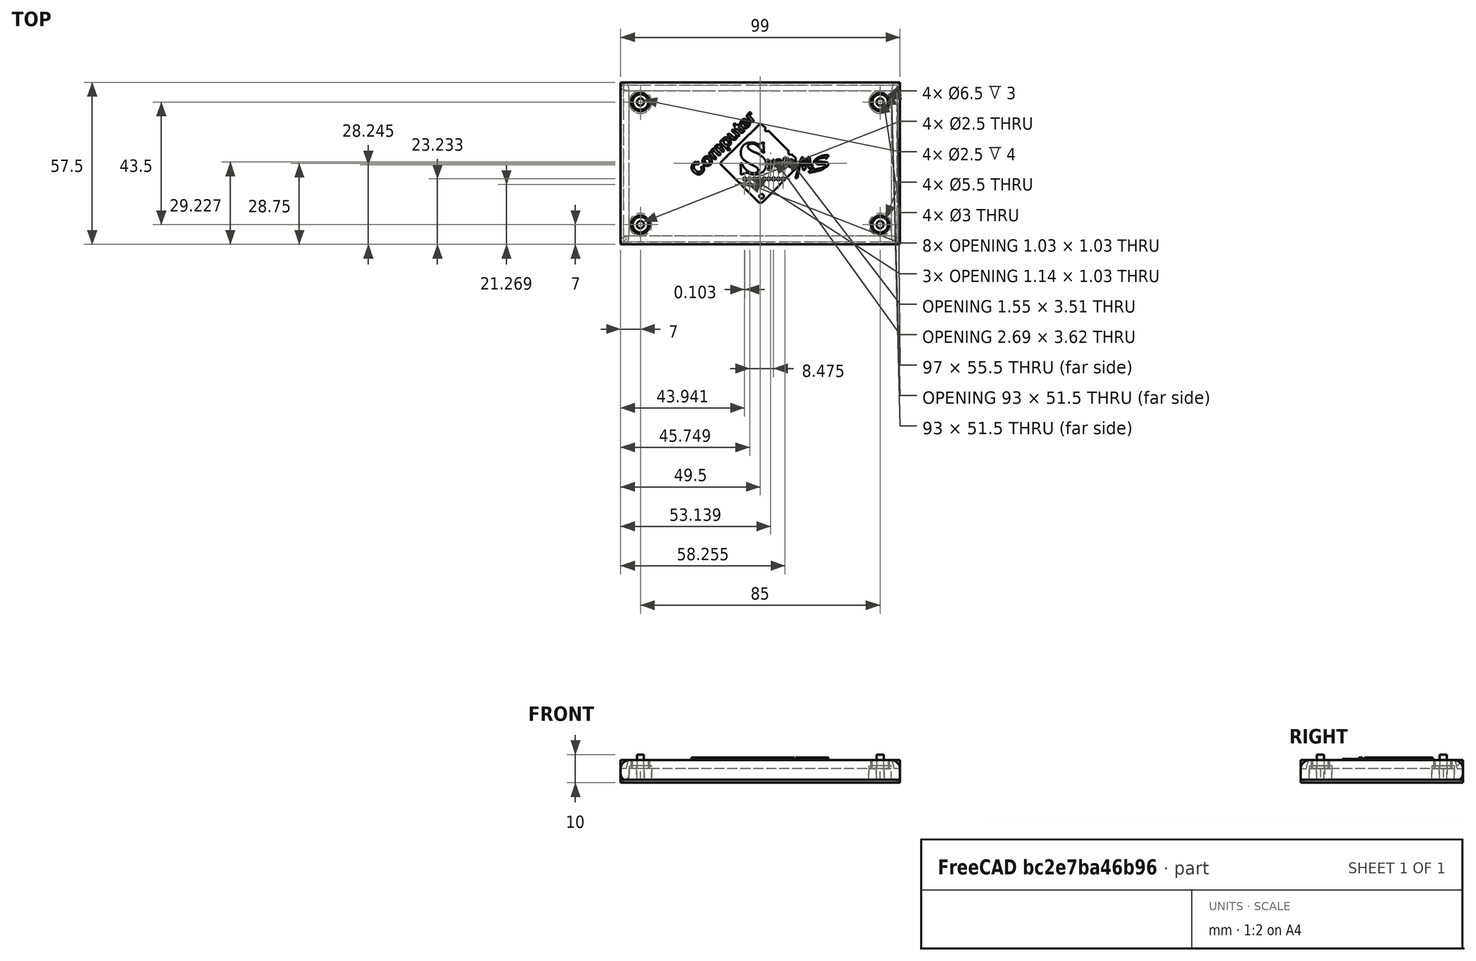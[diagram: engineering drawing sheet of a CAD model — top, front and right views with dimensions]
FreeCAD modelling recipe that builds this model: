
FCSTD DOCUMENT  (FreeCAD 0.15R4572 (Git))
Label: top2
License: All rights reserved
LicenseURL: http://en.wikipedia.org/wiki/All_rights_reserved
objects: Part::Feature×32, Part::Extrusion×32, Sketcher::SketchObject×10, Part::Cut×5, PartDesign::Pad×4, PartDesign::Fillet×4, PartDesign::Pocket×3, Part::Thickness×1, Part::MultiFuse×1
note: 99 computed .brp shape members not serialized (recipe doc carries the construction recipe); baked Part::Feature solids carry a one-line shape summary decoded from their .brp

FEATURE [Sketcher::SketchObject] Sketch  label="Отверстия под части корпуса"
  sketch-geometry (12):
    g0: LineSegment [constr] StartX=-42.5 StartY=21.75 StartZ=0 EndX=42.5 EndY=21.75 EndZ=0
    g1: LineSegment [constr] StartX=42.5 StartY=21.75 StartZ=0 EndX=42.5 EndY=-21.75 EndZ=0
    g2: LineSegment [constr] StartX=42.5 StartY=-21.75 StartZ=0 EndX=-42.5 EndY=-21.75 EndZ=0
    g3: LineSegment [constr] StartX=-42.5 StartY=-21.75 StartZ=0 EndX=-42.5 EndY=21.75 EndZ=0
    g4: Circle CenterX=-42.5 CenterY=21.75 CenterZ=0 NormalX=0 NormalY=0 NormalZ=1 Radius=1.5
    g5: Circle CenterX=-42.5 CenterY=21.75 CenterZ=0 NormalX=0 NormalY=0 NormalZ=1 Radius=4
    g6: Circle CenterX=-42.5 CenterY=-21.75 CenterZ=0 NormalX=0 NormalY=0 NormalZ=1 Radius=1.5
    g7: Circle CenterX=42.5 CenterY=-21.75 CenterZ=0 NormalX=0 NormalY=0 NormalZ=1 Radius=1.5
    g8: Circle CenterX=42.5 CenterY=21.75 CenterZ=0 NormalX=0 NormalY=0 NormalZ=1 Radius=1.5
    g9: Circle CenterX=-42.5 CenterY=-21.75 CenterZ=0 NormalX=0 NormalY=0 NormalZ=1 Radius=4
    g10: Circle CenterX=42.5 CenterY=-21.75 CenterZ=0 NormalX=0 NormalY=0 NormalZ=1 Radius=4
    g11: Circle CenterX=42.5 CenterY=21.75 CenterZ=0 NormalX=0 NormalY=0 NormalZ=1 Radius=4
  constraints (28):
    c: Coincident(g0,g1)
    c: Coincident(g1,g2)
    c: Coincident(g2,g3)
    c: Coincident(g3,g0)
    c: Horizontal(g0)
    c: Horizontal(g2)
    c: Vertical(g1)
    c: Vertical(g3)
    c: Symmetric(g1,g0,g-1)
    c: Symmetric(g0,g0,g-2)
    c: DistanceY(g1) = -43.5
    c: DistanceX(g0) = 85
    c: Coincident(g4,g0)
    c: Coincident(g5,g0)
    c: Coincident(g6,g2)
    c: Coincident(g7,g1)
    c: Coincident(g8,g0)
    c: Equal(g8,g7)
    c: Equal(g7,g6)
    c: Equal(g6,g4)
    c: Radius(g7) = 1.5
    c: Coincident(g9,g2)
    c: Coincident(g10,g1)
    c: Coincident(g11,g0)
    c: Equal(g11,g10)
    c: Equal(g10,g9)
    c: Equal(g9,g5)
    c: Radius(g9) = 4
FEATURE [Sketcher::SketchObject] Sketch001  label="Маска нижней части"
  sketch-geometry (8):
    g0: LineSegment [constr] StartX=-45 StartY=25 StartZ=0 EndX=45 EndY=25 EndZ=0
    g1: LineSegment [constr] StartX=45 StartY=25 StartZ=0 EndX=45 EndY=-25 EndZ=0
    g2: LineSegment [constr] StartX=45 StartY=-25 StartZ=0 EndX=-45 EndY=-25 EndZ=0
    g3: LineSegment [constr] StartX=-45 StartY=-25 StartZ=0 EndX=-45 EndY=25 EndZ=0
    g4: LineSegment StartX=-46.5 StartY=25.75 StartZ=0 EndX=46.5 EndY=25.75 EndZ=0
    g5: LineSegment StartX=46.5 StartY=25.75 StartZ=0 EndX=46.5 EndY=-25.75 EndZ=0
    g6: LineSegment StartX=46.5 StartY=-25.75 StartZ=0 EndX=-46.5 EndY=-25.75 EndZ=0
    g7: LineSegment StartX=-46.5 StartY=-25.75 StartZ=0 EndX=-46.5 EndY=25.75 EndZ=0
  constraints (24):
    c: Coincident(g0,g1)
    c: Coincident(g1,g2)
    c: Coincident(g2,g3)
    c: Coincident(g3,g0)
    c: Horizontal(g0)
    c: Horizontal(g2)
    c: Vertical(g1)
    c: Vertical(g3)
    c: Symmetric(g0,g0,g-2)
    c: Symmetric(g0,g1,g-1)
    c: DistanceX(g0) = 90
    c: DistanceY(g1) = -50
    c: Coincident(g4,g5)
    c: Coincident(g5,g6)
    c: Coincident(g6,g7)
    c: Coincident(g7,g4)
    c: Horizontal(g4)
    c: Horizontal(g6)
    c: Vertical(g5)
    c: Vertical(g7)
    c: Symmetric(g4,g5,g-1)
    c: Symmetric(g4,g4,g-2)
    c: DistanceY(g7) = 51.5
    c: DistanceX(g6) = -93
FEATURE [PartDesign::Pad] Pad
  Length = 4
  Length2 = 100
  Sketch = -> Sketch001
  Type = 0
FEATURE [Part::Thickness] Thickness
  Faces = -> Pad [Face5]
  Intersection = false
  Join = 2
  Mode = 0
  SelfIntersection = false
  Value = 3
FEATURE [PartDesign::Pad] Pad001
  Length = 5
  Length2 = 100
  Sketch = -> Sketch
  Type = 0
FEATURE [Sketcher::SketchObject] Sketch002  label="Отверстия под части корпуса001"
  Placement = pos=(0,0,7) rot=(0,0,1;0rad)
  Support = -> Thickness [Face11]
  sketch-geometry (8):
    g0: LineSegment [constr] StartX=-42.5 StartY=21.75 StartZ=0 EndX=42.5 EndY=21.75 EndZ=0
    g1: LineSegment [constr] StartX=42.5 StartY=21.75 StartZ=0 EndX=42.5 EndY=-21.75 EndZ=0
    g2: LineSegment [constr] StartX=42.5 StartY=-21.75 StartZ=0 EndX=-42.5 EndY=-21.75 EndZ=0
    g3: LineSegment [constr] StartX=-42.5 StartY=-21.75 StartZ=0 EndX=-42.5 EndY=21.75 EndZ=0
    g4: Circle CenterX=-42.5 CenterY=21.75 CenterZ=0 NormalX=0 NormalY=0 NormalZ=1 Radius=2.75
    g5: Circle CenterX=-42.5 CenterY=-21.75 CenterZ=0 NormalX=0 NormalY=0 NormalZ=1 Radius=2.75
    g6: Circle CenterX=42.5 CenterY=-21.75 CenterZ=0 NormalX=0 NormalY=0 NormalZ=1 Radius=2.75
    g7: Circle CenterX=42.5 CenterY=21.75 CenterZ=0 NormalX=0 NormalY=0 NormalZ=1 Radius=2.75
  constraints (20):
    c: Coincident(g0,g1)
    c: Coincident(g1,g2)
    c: Coincident(g2,g3)
    c: Coincident(g3,g0)
    c: Horizontal(g0)
    c: Horizontal(g2)
    c: Vertical(g1)
    c: Vertical(g3)
    c: Symmetric(g1,g0,g-1)
    c: Symmetric(g0,g0,g-2)
    c: DistanceY(g1) = -43.5
    c: DistanceX(g0) = 85
    c: Coincident(g4,g0)
    c: Coincident(g5,g2)
    c: Coincident(g6,g1)
    c: Coincident(g7,g0)
    c: Equal(g7,g6)
    c: Equal(g6,g5)
    c: Equal(g5,g4)
    c: Radius(g6) = 2.75
FEATURE [PartDesign::Pocket] Pocket
  Length = 3.5
  Sketch = -> Sketch002
  Type = 0
FEATURE [Part::Feature] Face
  shape: bbox 1.861 x 1.858 x 2e-07 mm, 1 faces, 0 solids (baked)
FEATURE [Part::Feature] Face001
  shape: bbox 9.096 x 11.37 x 2e-07 mm, 1 faces, 0 solids (baked)
FEATURE [Part::Feature] Face002
  shape: bbox 1.758 x 1.861 x 2e-07 mm, 1 faces, 0 solids (baked)
FEATURE [Part::Feature] Face003
  shape: bbox 1.035 x 1.032 x 2e-07 mm, 1 faces, 0 solids (baked)
FEATURE [Part::Feature] Face004
  shape: bbox 1.035 x 1.032 x 2e-07 mm, 1 faces, 0 solids (baked)
FEATURE [Part::Feature] Face005
  shape: bbox 1.138 x 1.032 x 2e-07 mm, 1 faces, 0 solids (baked)
FEATURE [Part::Feature] Face006
  shape: bbox 1.032 x 1.032 x 2e-07 mm, 1 faces, 0 solids (baked)
FEATURE [Part::Feature] Face007
  shape: bbox 1.035 x 1.032 x 2e-07 mm, 1 faces, 0 solids (baked)
FEATURE [Part::Feature] Face008
  shape: bbox 4.445 x 4.548 x 2e-07 mm, 1 faces, 0 solids (baked)
FEATURE [Part::Extrusion] Extrude003
  Base = -> Face005
  Dir = (0,0,1)
  Solid = false
FEATURE [Part::Extrusion] Extrude004
  Base = -> Face004
  Dir = (0,0,1)
  Solid = false
FEATURE [Part::Extrusion] Extrude005
  Base = -> Face006
  Dir = (0,0,1)
  Solid = false
FEATURE [Part::Extrusion] Extrude010
  Base = -> Face007
  Dir = (0,0,1)
  Solid = false
FEATURE [Part::Extrusion] Extrude012
  Base = -> Face
  Dir = (0,0,1)
  Solid = false
FEATURE [Part::Extrusion] Extrude013  label="C"
  Base = -> Face008
  Dir = (0,0,1)
  Solid = true
FEATURE [Part::Feature] Face009
  shape: bbox 3.431 x 3.472 x 2e-07 mm, 1 faces, 0 solids (baked)
FEATURE [Part::Extrusion] Extrude
  Base = -> Face009
  Dir = (0,0,1)
  Solid = false
FEATURE [Part::Feature] Face010
  shape: bbox 5.686 x 5.271 x 2e-07 mm, 1 faces, 0 solids (baked)
FEATURE [Part::Extrusion] Extrude014  label="M"
  Base = -> Face010
  Dir = (0,0,1)
  Solid = false
FEATURE [Part::Cut] Cut  label="O"
  Base = -> Extrude
  Tool = -> Extrude012
FEATURE [Part::Feature] Face011
  shape: bbox 6.013 x 7.647 x 2e-07 mm, 1 faces, 0 solids (baked)
FEATURE [Part::Feature] Face012
  shape: bbox 6.923 x 6.2 x 2e-07 mm, 1 faces, 0 solids (baked)
FEATURE [Part::Feature] Face013
  shape: bbox 1.032 x 0.6202 x 2e-07 mm, 1 faces, 0 solids (baked)
FEATURE [Part::Feature] Face014
  shape: bbox 2.375 x 2.687 x 2e-07 mm, 1 faces, 0 solids (baked)
FEATURE [Part::Feature] Face015
  shape: bbox 1.549 x 3.513 x 2e-07 mm, 1 faces, 0 solids (baked)
FEATURE [Part::Feature] Face016
  shape: bbox 2.478 x 2.687 x 2e-07 mm, 1 faces, 0 solids (baked)
FEATURE [Part::Feature] Face017
  shape: bbox 2.687 x 3.619 x 2e-07 mm, 1 faces, 0 solids (baked)
FEATURE [Part::Extrusion] Extrude015  label="S"
  Base = -> Face001
  Dir = (0,0,1)
  Solid = false
FEATURE [Part::Extrusion] Extrude016  label="S002"
  Base = -> Face016
  Dir = (0,0,1)
  Solid = false
FEATURE [Part::Extrusion] Extrude017
  Base = -> Face014
  Dir = (0,0,1)
  Solid = false
FEATURE [Part::Extrusion] Extrude018
  Base = -> Face013
  Dir = (0,0,1)
  Solid = false
FEATURE [Part::Extrusion] Extrude019
  Base = -> Face002
  Dir = (0,0,1)
  Solid = false
FEATURE [Part::Extrusion] Extrude020  label="S001"
  Base = -> Face012
  Dir = (0,0,1)
  Solid = false
FEATURE [Part::Extrusion] Extrude022  label="T001"
  Base = -> Face015
  Dir = (0,0,1)
  Solid = false
FEATURE [Part::Extrusion] Extrude023  label="M001"
  Base = -> Face011
  Dir = (0,0,1)
  Solid = false
FEATURE [Part::Extrusion] Extrude024  label="Y"
  Base = -> Face017
  Dir = (0,0,1)
  Solid = false
FEATURE [Part::Feature] Face018
  shape: bbox 26.62 x 28.11 x 2e-07 mm, 1 faces, 0 solids (baked)
FEATURE [Part::Extrusion] Extrude001
  Base = -> Face018
  Dir = (0,0,0.5)
  Solid = false
FEATURE [Part::Feature] Face019
  shape: bbox 3.97 x 4.859 x 2e-07 mm, 1 faces, 0 solids (baked)
FEATURE [Part::Extrusion] Extrude021
  Base = -> Face019
  Dir = (0,0,1)
  Solid = false
FEATURE [Part::Feature] Face020
  shape: bbox 1.964 x 1.964 x 2e-07 mm, 1 faces, 0 solids (baked)
FEATURE [Part::Extrusion] Extrude007
  Base = -> Face020
  Dir = (0,0,1)
  Solid = false
FEATURE [Part::Cut] Cut001  label="P"
  Base = -> Extrude021
  Tool = -> Extrude019
FEATURE [Part::Cut] Cut002
  Base = -> Extrude001
  Tool = -> Extrude007
FEATURE [Part::Cut] Cut004  label="E001"
  Base = -> Extrude017
  Tool = -> Extrude018
FEATURE [Part::Feature] Face021
  shape: bbox 4.342 x 3.928 x 2e-07 mm, 1 faces, 0 solids (baked)
FEATURE [Part::Extrusion] Extrude011  label="U"
  Base = -> Face021
  Dir = (0,0,1)
  Solid = false
FEATURE [Part::Feature] Face022
  shape: bbox 3.822 x 3.513 x 2e-07 mm, 1 faces, 0 solids (baked)
FEATURE [Part::Extrusion] Extrude006  label="T"
  Base = -> Face022
  Dir = (0,0,1)
  Solid = false
FEATURE [Part::Feature] Face023
  shape: bbox 3.41 x 3.39 x 2e-07 mm, 1 faces, 0 solids (baked)
FEATURE [Part::Extrusion] Extrude008
  Base = -> Face023
  Dir = (0,0,1)
  Solid = false
FEATURE [Part::Feature] Face024
  shape: bbox 1.138 x 1.241 x 2e-07 mm, 1 faces, 0 solids (baked)
FEATURE [Part::Extrusion] Extrude009
  Base = -> Face024
  Dir = (0,0,1)
  Solid = false
FEATURE [Part::Cut] Cut003  label="E"
  Base = -> Extrude008
  Tool = -> Extrude009
FEATURE [Part::Feature] Face025
  shape: bbox 2.896 x 3.719 x 2e-07 mm, 1 faces, 0 solids (baked)
FEATURE [Part::Extrusion] Extrude002  label="R"
  Base = -> Face025
  Dir = (0,0,1)
  Solid = false
FEATURE [Part::Feature] Face026
  shape: bbox 1.035 x 1.032 x 2e-07 mm, 1 faces, 0 solids (baked)
FEATURE [Part::Feature] Face027
  shape: bbox 1.032 x 1.032 x 2e-07 mm, 1 faces, 0 solids (baked)
FEATURE [Part::Feature] Face028
  shape: bbox 1.138 x 1.032 x 2e-07 mm, 1 faces, 0 solids (baked)
FEATURE [Part::Feature] Face029
  shape: bbox 1.032 x 1.032 x 2e-07 mm, 1 faces, 0 solids (baked)
FEATURE [Part::Feature] Face030
  shape: bbox 1.138 x 1.032 x 2e-07 mm, 1 faces, 0 solids (baked)
FEATURE [Part::Feature] Face031
  shape: bbox 1.032 x 1.032 x 2e-07 mm, 1 faces, 0 solids (baked)
FEATURE [Part::Extrusion] Extrude025
  Base = -> Face031
  Dir = (0,0,1)
  Solid = false
FEATURE [Part::Extrusion] Extrude026
  Base = -> Face030
  Dir = (0,0,1)
  Solid = false
FEATURE [Part::Extrusion] Extrude027
  Base = -> Face029
  Dir = (0,0,1)
  Solid = false
FEATURE [Part::Extrusion] Extrude028
  Base = -> Face028
  Dir = (0,0,1)
  Solid = false
FEATURE [Part::Extrusion] Extrude029
  Base = -> Face027
  Dir = (0,0,1)
  Solid = false
FEATURE [Part::Extrusion] Extrude030
  Base = -> Face026
  Dir = (0,0,1)
  Solid = false
FEATURE [Part::Extrusion] Extrude031
  Base = -> Face003
  Dir = (0,0,1)
  Solid = false
FEATURE [Part::MultiFuse] Fusion
  Placement = pos=(-94,191,6.9) rot=(0,0,1;0rad)
  Shapes = -> [Extrude002,Extrude024,Extrude029,Extrude023,Extrude025,Extrude027,Extrude026,Extrude030,Extrude028,Extrude031,Cut002,Cut003,Cut004,Cut,Cut001,Extrude013,Extrude016,Extrude022,Extrude005,Extrude020,Extrude004,Extrude003,Extrude014,Extrude010,Extrude006,Extrude015,Extrude011]
FEATURE [Sketcher::SketchObject] Sketch003
  Placement = pos=(0,0,7) rot=(0,0,1;0rad)
  Support = -> Pocket [Face15]
  sketch-geometry (6):
    g0: LineSegment StartX=-48.8866 StartY=28.9301 StartZ=0 EndX=46.8488 EndY=28.9301 EndZ=0
    g1: LineSegment StartX=46.8488 StartY=28.9301 StartZ=0 EndX=46.8488 EndY=-28.4828 EndZ=0
    g2: LineSegment StartX=46.8488 StartY=-28.4828 StartZ=0 EndX=-48.8866 EndY=-28.4828 EndZ=0
    g3: LineSegment StartX=-48.8866 StartY=-28.4828 StartZ=0 EndX=-48.8866 EndY=28.9301 EndZ=0
    g4: LineSegment StartX=-48.8866 StartY=0 StartZ=0 EndX=46.8488 EndY=0 EndZ=0
    g5: LineSegment StartX=0 StartY=28.9301 StartZ=0 EndX=0 EndY=-28.4828 EndZ=0
  constraints (14):
    c: Coincident(g0,g1)
    c: Coincident(g1,g2)
    c: Coincident(g2,g3)
    c: Coincident(g3,g0)
    c: Horizontal(g0)
    c: Horizontal(g2)
    c: Vertical(g1)
    c: Vertical(g3)
    c: PointOnObject(g4,g3)
    c: PointOnObject(g4,g1)
    c: Horizontal(g4)
    c: PointOnObject(g5,g0)
    c: PointOnObject(g5,g2)
    c: Vertical(g5)
FEATURE [Sketcher::SketchObject] Sketch004
  Placement = pos=(-94,191,7.4) rot=(0,0,1;0rad)
  Support = -> Fusion [Face70]
FEATURE [Sketcher::SketchObject] Sketch005
  Placement = pos=(-94,191,7.4) rot=(0,0,1;0rad)
  Support = -> Fusion [Face70]
  sketch-geometry (4):
    g0: LineSegment StartX=69.5836 StartY=-172.746 StartZ=0 EndX=118.185 EndY=-172.746 EndZ=0
    g1: LineSegment StartX=118.185 StartY=-172.746 StartZ=0 EndX=118.185 EndY=-205.174 EndZ=0
    g2: LineSegment StartX=118.185 StartY=-205.174 StartZ=0 EndX=69.5836 EndY=-205.174 EndZ=0
    g3: LineSegment StartX=69.5836 StartY=-205.174 StartZ=0 EndX=69.5836 EndY=-172.746 EndZ=0
  constraints (8):
    c: Coincident(g0,g1)
    c: Coincident(g1,g2)
    c: Coincident(g2,g3)
    c: Coincident(g3,g0)
    c: Horizontal(g0)
    c: Horizontal(g2)
    c: Vertical(g1)
    c: Vertical(g3)
FEATURE [PartDesign::Fillet] Fillet
  Base = -> Pocket [Edge23,Edge25,Edge28,Edge26]
  Radius = 3
FEATURE [PartDesign::Fillet] Fillet001
  Base = -> Fillet [Edge1,Edge7,Edge17,Edge4]
  Radius = 2
FEATURE [Sketcher::SketchObject] Sketch006  label="Маска нижней части001"
  Placement = pos=(0,0,0) rot=(1,0,0;3.14159rad)
  Support = -> Thickness [Face6]
  sketch-geometry (8):
    g0: LineSegment StartX=-48.5 StartY=27.75 StartZ=0 EndX=48.5 EndY=27.75 EndZ=0
    g1: LineSegment StartX=48.5 StartY=27.75 StartZ=0 EndX=48.5 EndY=-27.75 EndZ=0
    g2: LineSegment StartX=48.5 StartY=-27.75 StartZ=0 EndX=-48.5 EndY=-27.75 EndZ=0
    g3: LineSegment StartX=-48.5 StartY=-27.75 StartZ=0 EndX=-48.5 EndY=27.75 EndZ=0
    g4: LineSegment StartX=-49.5 StartY=28.75 StartZ=0 EndX=49.5 EndY=28.75 EndZ=0
    g5: LineSegment StartX=49.5 StartY=28.75 StartZ=0 EndX=49.5 EndY=-28.75 EndZ=0
    g6: LineSegment StartX=49.5 StartY=-28.75 StartZ=0 EndX=-49.5 EndY=-28.75 EndZ=0
    g7: LineSegment StartX=-49.5 StartY=-28.75 StartZ=0 EndX=-49.5 EndY=28.75 EndZ=0
  constraints (24):
    c: Coincident(g0,g1)
    c: Coincident(g1,g2)
    c: Coincident(g2,g3)
    c: Coincident(g3,g0)
    c: Horizontal(g0)
    c: Horizontal(g2)
    c: Vertical(g1)
    c: Vertical(g3)
    c: Symmetric(g0,g0,g-2)
    c: Symmetric(g0,g1,g-1)
    c: DistanceX(g0) = 97
    c: DistanceY(g1) = -55.5
    c: Coincident(g4,g5)
    c: Coincident(g5,g6)
    c: Coincident(g6,g7)
    c: Coincident(g7,g4)
    c: Horizontal(g4)
    c: Horizontal(g6)
    c: Vertical(g5)
    c: Vertical(g7)
    c: Symmetric(g4,g5,g-1)
    c: Symmetric(g4,g4,g-2)
    c: DistanceY(g7) = 57.5
    c: DistanceX(g6) = -99
FEATURE [PartDesign::Pad] Pad002
  Length = 1
  Length2 = 100
  Sketch = -> Sketch006
  Type = 0
FEATURE [Sketcher::SketchObject] Sketch007  label="Отверстия под части корпуса002"
  Placement = pos=(0,0,4) rot=(1,0,0;3.14159rad)
  Support = -> Pad002 [Face5]
  sketch-geometry (12):
    g0: LineSegment [constr] StartX=-42.5 StartY=21.75 StartZ=0 EndX=42.5 EndY=21.75 EndZ=0
    g1: LineSegment [constr] StartX=42.5 StartY=21.75 StartZ=0 EndX=42.5 EndY=-21.75 EndZ=0
    g2: LineSegment [constr] StartX=42.5 StartY=-21.75 StartZ=0 EndX=-42.5 EndY=-21.75 EndZ=0
    g3: LineSegment [constr] StartX=-42.5 StartY=-21.75 StartZ=0 EndX=-42.5 EndY=21.75 EndZ=0
    g4: Circle CenterX=-42.5 CenterY=21.75 CenterZ=0 NormalX=0 NormalY=0 NormalZ=1 Radius=1.25
    g5: Circle CenterX=-42.5 CenterY=21.75 CenterZ=0 NormalX=0 NormalY=0 NormalZ=1 Radius=4
    g6: Circle CenterX=-42.5 CenterY=-21.75 CenterZ=0 NormalX=0 NormalY=0 NormalZ=1 Radius=1.25
    g7: Circle CenterX=42.5 CenterY=-21.75 CenterZ=0 NormalX=0 NormalY=0 NormalZ=1 Radius=1.25
    g8: Circle CenterX=42.5 CenterY=21.75 CenterZ=0 NormalX=0 NormalY=0 NormalZ=1 Radius=1.25
    g9: Circle CenterX=-42.5 CenterY=-21.75 CenterZ=0 NormalX=0 NormalY=0 NormalZ=1 Radius=4
    g10: Circle CenterX=42.5 CenterY=-21.75 CenterZ=0 NormalX=0 NormalY=0 NormalZ=1 Radius=4
    g11: Circle CenterX=42.5 CenterY=21.75 CenterZ=0 NormalX=0 NormalY=0 NormalZ=1 Radius=4
  constraints (28):
    c: Coincident(g0,g1)
    c: Coincident(g1,g2)
    c: Coincident(g2,g3)
    c: Coincident(g3,g0)
    c: Horizontal(g0)
    c: Horizontal(g2)
    c: Vertical(g1)
    c: Vertical(g3)
    c: Symmetric(g1,g0,g-1)
    c: Symmetric(g0,g0,g-2)
    c: DistanceY(g1) = -43.5
    c: DistanceX(g0) = 85
    c: Coincident(g4,g0)
    c: Coincident(g5,g0)
    c: Coincident(g6,g2)
    c: Coincident(g7,g1)
    c: Coincident(g8,g0)
    c: Equal(g8,g7)
    c: Equal(g7,g6)
    c: Equal(g6,g4)
    c: Radius(g7) = 1.25
    c: Coincident(g9,g2)
    c: Coincident(g10,g1)
    c: Coincident(g11,g0)
    c: Equal(g11,g10)
    c: Equal(g10,g9)
    c: Equal(g9,g5)
    c: Radius(g9) = 4
FEATURE [PartDesign::Pad] Pad003
  Length = 4
  Length2 = 100
  Sketch = -> Sketch007
  Type = 0
FEATURE [Sketcher::SketchObject] Sketch008  label="Отверстия под части корпуса003"
  Placement = pos=(0,0,4) rot=(1,0,0;3.14159rad)
  Support = -> Pad003 [Face24]
  sketch-geometry (12):
    g0: LineSegment [constr] StartX=-42.5 StartY=21.75 StartZ=0 EndX=42.5 EndY=21.75 EndZ=0
    g1: LineSegment [constr] StartX=42.5 StartY=21.75 StartZ=0 EndX=42.5 EndY=-21.75 EndZ=0
    g2: LineSegment [constr] StartX=42.5 StartY=-21.75 StartZ=0 EndX=-42.5 EndY=-21.75 EndZ=0
    g3: LineSegment [constr] StartX=-42.5 StartY=-21.75 StartZ=0 EndX=-42.5 EndY=21.75 EndZ=0
    g4: Circle CenterX=-42.5 CenterY=21.75 CenterZ=0 NormalX=0 NormalY=0 NormalZ=1 Radius=1.25
    g5: Circle [constr] CenterX=-42.5 CenterY=21.75 CenterZ=0 NormalX=0 NormalY=0 NormalZ=1 Radius=4
    g6: Circle CenterX=-42.5 CenterY=-21.75 CenterZ=0 NormalX=0 NormalY=0 NormalZ=1 Radius=1.25
    g7: Circle CenterX=42.5 CenterY=-21.75 CenterZ=0 NormalX=0 NormalY=0 NormalZ=1 Radius=1.25
    g8: Circle CenterX=42.5 CenterY=21.75 CenterZ=0 NormalX=0 NormalY=0 NormalZ=1 Radius=1.25
    g9: Circle [constr] CenterX=-42.5 CenterY=-21.75 CenterZ=0 NormalX=0 NormalY=0 NormalZ=1 Radius=4
    g10: Circle [constr] CenterX=42.5 CenterY=-21.75 CenterZ=0 NormalX=0 NormalY=0 NormalZ=1 Radius=4
    g11: Circle [constr] CenterX=42.5 CenterY=21.75 CenterZ=0 NormalX=0 NormalY=0 NormalZ=1 Radius=4
  constraints (28):
    c: Coincident(g0,g1)
    c: Coincident(g1,g2)
    c: Coincident(g2,g3)
    c: Coincident(g3,g0)
    c: Horizontal(g0)
    c: Horizontal(g2)
    c: Vertical(g1)
    c: Vertical(g3)
    c: Symmetric(g1,g0,g-1)
    c: Symmetric(g0,g0,g-2)
    c: DistanceY(g1) = -43.5
    c: DistanceX(g0) = 85
    c: Coincident(g4,g0)
    c: Coincident(g5,g0)
    c: Coincident(g6,g2)
    c: Coincident(g7,g1)
    c: Coincident(g8,g0)
    c: Equal(g8,g7)
    c: Equal(g7,g6)
    c: Equal(g6,g4)
    c: Radius(g7) = 1.25
    c: Coincident(g9,g2)
    c: Coincident(g10,g1)
    c: Coincident(g11,g0)
    c: Equal(g11,g10)
    c: Equal(g10,g9)
    c: Equal(g9,g5)
    c: Radius(g9) = 4
FEATURE [PartDesign::Pocket] Pocket001
  Length = 5
  Sketch = -> Sketch008
  Type = 0
FEATURE [Sketcher::SketchObject] Sketch009  label="Отверстия под части корпуса004"
  Placement = pos=(0,0,7) rot=(0,0,1;0rad)
  Support = -> Pocket001 [Face42]
  sketch-geometry (12):
    g0: LineSegment [constr] StartX=-42.5 StartY=21.75 StartZ=0 EndX=42.5 EndY=21.75 EndZ=0
    g1: LineSegment [constr] StartX=42.5 StartY=21.75 StartZ=0 EndX=42.5 EndY=-21.75 EndZ=0
    g2: LineSegment [constr] StartX=42.5 StartY=-21.75 StartZ=0 EndX=-42.5 EndY=-21.75 EndZ=0
    g3: LineSegment [constr] StartX=-42.5 StartY=-21.75 StartZ=0 EndX=-42.5 EndY=21.75 EndZ=0
    g4: Circle [constr] CenterX=-42.5 CenterY=21.75 CenterZ=0 NormalX=0 NormalY=0 NormalZ=1 Radius=1.25
    g5: Circle CenterX=-42.5 CenterY=21.75 CenterZ=0 NormalX=0 NormalY=0 NormalZ=1 Radius=3.25
    g6: Circle [constr] CenterX=-42.5 CenterY=-21.75 CenterZ=0 NormalX=0 NormalY=0 NormalZ=1 Radius=1.25
    g7: Circle [constr] CenterX=42.5 CenterY=-21.75 CenterZ=0 NormalX=0 NormalY=0 NormalZ=1 Radius=1.25
    g8: Circle [constr] CenterX=42.5 CenterY=21.75 CenterZ=0 NormalX=0 NormalY=0 NormalZ=1 Radius=1.25
    g9: Circle CenterX=-42.5 CenterY=-21.75 CenterZ=0 NormalX=0 NormalY=0 NormalZ=1 Radius=3.25
    g10: Circle CenterX=42.5 CenterY=-21.75 CenterZ=0 NormalX=0 NormalY=0 NormalZ=1 Radius=3.25
    g11: Circle CenterX=42.5 CenterY=21.75 CenterZ=0 NormalX=0 NormalY=0 NormalZ=1 Radius=3.25
  constraints (28):
    c: Coincident(g0,g1)
    c: Coincident(g1,g2)
    c: Coincident(g2,g3)
    c: Coincident(g3,g0)
    c: Horizontal(g0)
    c: Horizontal(g2)
    c: Vertical(g1)
    c: Vertical(g3)
    c: Symmetric(g1,g0,g-1)
    c: Symmetric(g0,g0,g-2)
    c: DistanceY(g1) = -43.5
    c: DistanceX(g0) = 85
    c: Coincident(g4,g0)
    c: Coincident(g5,g0)
    c: Coincident(g6,g2)
    c: Coincident(g7,g1)
    c: Coincident(g8,g0)
    c: Equal(g8,g7)
    c: Equal(g7,g6)
    c: Equal(g6,g4)
    c: Radius(g7) = 1.25
    c: Coincident(g9,g2)
    c: Coincident(g10,g1)
    c: Coincident(g11,g0)
    c: Equal(g11,g10)
    c: Equal(g10,g9)
    c: Equal(g9,g5)
    c: Radius(g9) = 3.25
FEATURE [PartDesign::Pocket] Pocket002
  Length = 3
  Sketch = -> Sketch009
  Type = 0
FEATURE [PartDesign::Fillet] Fillet002
  Base = -> Pocket002 [Edge75,Edge57,Edge77,Edge59,Edge71,Edge53,Edge72,Edge55]
  Radius = 2
FEATURE [PartDesign::Fillet] Fillet003
  Base = -> Fillet002 [Edge52,Edge50,Edge46,Edge42,Edge39,Edge40,Edge44,Edge49]
  Radius = 3
